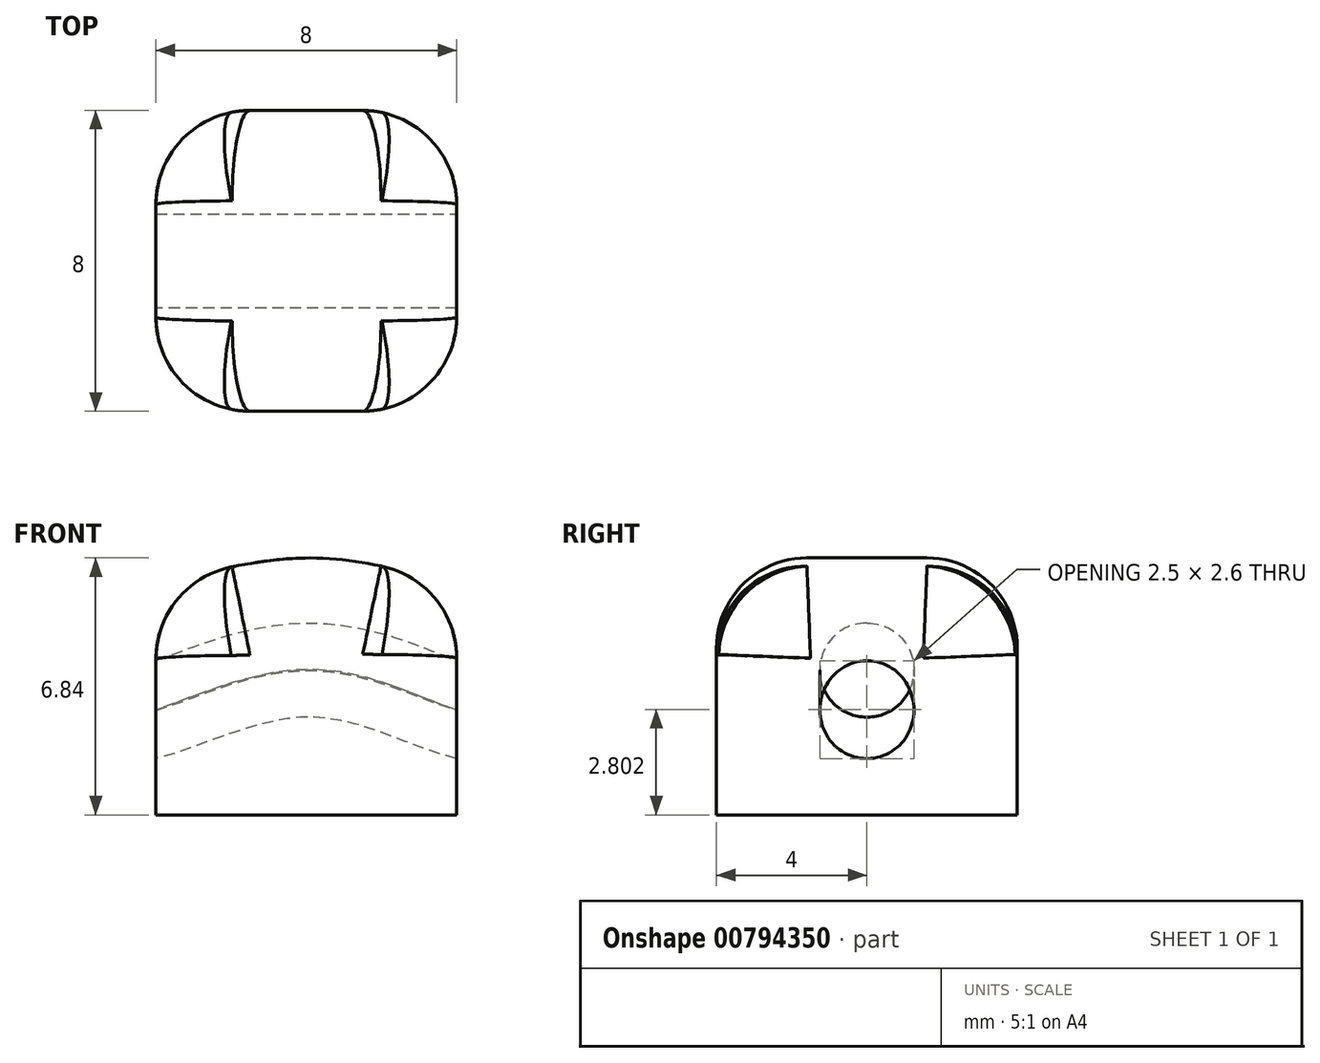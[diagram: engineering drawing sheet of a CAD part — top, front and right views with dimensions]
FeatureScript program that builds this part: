
annotation { "Feature Type Name" : "Feature", "Feature Type Description" : "" }
export const myFeature = defineFeature(function(context is Context, id is Id, definition is map)
    precondition{}
    {
        {
            var Q0;
            Q0=qCreatedBy(makeId("Front.planeOp"),FACE);
            var sketch = newSketch(context, id + "F0", { "sketchPlane" : qUnion([Q0])});
            skLineSegment(sketch, "E0.bottom", {"start": v(4, 10) * mm, "end": v(-4, 10) * mm, "construction": true});
            skLineSegment(sketch, "E0.top", {"start": v(4, -10) * mm, "end": v(-4, -10) * mm});
            skLineSegment(sketch, "E0.left", {"start": v(4, 10) * mm, "end": v(4, -10) * mm});
            skLineSegment(sketch, "E0.right", {"start": v(-4, 10) * mm, "end": v(-4, -10) * mm});
            skLineSegment(sketch, "E1", {"start": v(0, 10) * mm, "end": v(0, -10) * mm, "construction": true});
            skPoint(sketch, "E2", {"position": v(0, 0) * mm});
            skFitSpline(sketch, "E3", {"points": [v(4, -8.5) * mm, v(0, -7.4) * mm, v(-4, -8.5) * mm], "startDerivative": vector(-8.01, 1.98) * mm, "endDerivative": vector(-6.11, -1.33) * mm});
            skFitSpline(sketch, "E4.0", {"points": [v(4.6, -6.07) * mm, v(4.4, -6.02) * mm, v(3.92, -5.87) * mm, v(3.1, -5.54) * mm, v(2.28, -5.26) * mm, v(1.6, -5.07) * mm, v(0.95, -4.95) * mm, v(0.4, -4.9) * mm, v(-0.05, -4.9) * mm, v(-0.49, -4.92) * mm, v(-0.9, -4.97) * mm, v(-1.3, -5.04) * mm, v(-1.8, -5.15) * mm, v(-2.37, -5.31) * mm, v(-2.99, -5.52) * mm, v(-3.53, -5.72) * mm, v(-4, -5.9) * mm, v(-4.36, -6.01) * mm, v(-4.5, -6.05) * mm, v(-4.53, -6.06) * mm]});
            skFitSpline(sketch, "E5", {"points": [v(-4, -3.89) * mm, v(0, -3.16) * mm, v(4, -3.89) * mm], "startDerivative": vector(5.39, 1.32) * mm, "endDerivative": vector(6.83, -1.78) * mm});
            skSolve(sketch);
        }
        {
            var Q0;
            {var subQ0=sQuery(id+"F0.wireOp",EDGE,"E0.top");Q0=makeQuery(id+"F0.imprint","IMPRINT",FACE,{"disambiguationData":[TD([[makeQuery(id+"F0.imprint","IMPRINT",EDGE,{"derivedFrom":subQ0}),-1.0]])]});}
            var Q1;
            {var subQ0=sQuery(id+"F0.wireOp",EDGE,"E4.0");Q1=makeQuery(id+"F0.imprint","IMPRINT",FACE,{"disambiguationData":[TD([[makeQuery(id+"F0.imprint","IMPRINT",EDGE,{"derivedFrom":subQ0}),-1.0]])]});}
            var Q2;
            {var subQ0=sQuery(id+"F0.wireOp",EDGE,"E3");Q2=makeQuery(id+"F0.imprint","IMPRINT",FACE,{"disambiguationData":[TD([[makeQuery(id+"F0.imprint","IMPRINT",EDGE,{"derivedFrom":subQ0}),-1.0]])]});}
            extrude(context, id + "F1", {"entities" : qUnion([Q0, Q1, Q2]), "endBound" : BoundingType.SYMMETRIC, "depth" : 8 * mm, "offsetDistance" : 25 * mm});
        }
        {
            var Q0;
            {var subQ0=sQuery(id+"F0.wireOp",EDGE,"E3");Q0=makeQuery(id+"F0.imprint","IMPRINT",FACE,{"disambiguationData":[TD([[makeQuery(id+"F0.imprint","IMPRINT",EDGE,{"derivedFrom":subQ0}),-1.0]])]});}
            extrude(context, id + "F2", {"entities" : qUnion([Q0]), "operationType" : NewBodyOperationType.REMOVE, "endBound" : BoundingType.SYMMETRIC, "oppositeDirection" : true, "depth" : 2.5 * mm, "offsetDistance" : 25 * mm});
        }
        {
            var Q0;
            Q0=makeQuery(id+"F2.boolean.opBoolean","COPY",EDGE,{"derivedFrom":makeQuery(id+"F2.opExtrude","CAP_EDGE",EDGE,{"disambiguationData":[OSD([sQuery(id+"F0.wireOp",EDGE,"E4.0")])],"isStart":false})});
            var Q1;
            Q1=makeQuery(id+"F2.boolean.opBoolean","COPY",EDGE,{"derivedFrom":makeQuery(id+"F2.opExtrude","CAP_EDGE",EDGE,{"disambiguationData":[OSD([sQuery(id+"F0.wireOp",EDGE,"E4.0")])],"isStart":true})});
            var Q2;
            Q2=makeQuery(id+"F2.boolean.opBoolean","COPY",EDGE,{"derivedFrom":makeQuery(id+"F2.opExtrude","CAP_EDGE",EDGE,{"disambiguationData":[OSD([sQuery(id+"F0.wireOp",EDGE,"E3")])],"isStart":true})});
            var Q3;
            Q3=makeQuery(id+"F2.boolean.opBoolean","COPY",EDGE,{"derivedFrom":makeQuery(id+"F2.opExtrude","CAP_EDGE",EDGE,{"disambiguationData":[OSD([sQuery(id+"F0.wireOp",EDGE,"E3")])],"isStart":false})});
            fillet(context, id + "F3", {"entities" : qUnion([Q0, Q1, Q2, Q3]), "radius" : 1.24 * mm, "tangentPropagation" : true, "allowEdgeOverflow" : false});
        }
        {
            var Q0;
            Q0=makeQuery(id+"F1.opExtrude","CAP_EDGE",EDGE,{"disambiguationData":[OSD([sQuery(id+"F0.wireOp",EDGE,"E5")])],"isStart":false});
            var Q1;
            Q1=makeQuery(id+"F1.opExtrude","CAP_EDGE",EDGE,{"disambiguationData":[OSD([sQuery(id+"F0.wireOp",EDGE,"E5")])],"isStart":true});
            fillet(context, id + "F4", {"entities" : qUnion([Q0, Q1]), "radius" : 2.4 * mm, "tangentPropagation" : true, "allowEdgeOverflow" : false});
        }
        {
            var Q0;
            Q0=makeQuery(id+"F1.opExtrude","CAP_EDGE",EDGE,{"disambiguationData":[OSD([sQuery(id+"F0.wireOp",EDGE,"E0.right")])],"isStart":false});
            var Q1;
            Q1=makeQuery(id+"F4.opFillet","BLEND_EDGE",EDGE,{"blendedFrom":[makeQuery(id+"F1.opExtrude","CAP_EDGE",EDGE,{"disambiguationData":[OSD([sQuery(id+"F0.wireOp",EDGE,"E5")])],"isStart":false}),makeQuery(id+"F1.opExtrude","SWEPT_FACE",FACE,{"disambiguationData":[OSD([sQuery(id+"F0.wireOp",EDGE,"E0.right")])]})],"blendedInto":[makeQuery(id+"F1.opExtrude","SWEPT_FACE",FACE,{"disambiguationData":[OSD([sQuery(id+"F0.wireOp",EDGE,"E0.right")])]})]});
            var Q2;
            Q2=makeQuery(id+"F1.opExtrude","CAP_EDGE",EDGE,{"disambiguationData":[OSD([sQuery(id+"F0.wireOp",EDGE,"E0.right")])],"isStart":true});
            var Q3;
            Q3=makeQuery(id+"F4.opFillet","BLEND_EDGE",EDGE,{"blendedFrom":[makeQuery(id+"F1.opExtrude","CAP_EDGE",EDGE,{"disambiguationData":[OSD([sQuery(id+"F0.wireOp",EDGE,"E5")])],"isStart":true}),makeQuery(id+"F1.opExtrude","SWEPT_FACE",FACE,{"disambiguationData":[OSD([sQuery(id+"F0.wireOp",EDGE,"E0.right")])]})],"blendedInto":[makeQuery(id+"F1.opExtrude","SWEPT_FACE",FACE,{"disambiguationData":[OSD([sQuery(id+"F0.wireOp",EDGE,"E0.right")])]})]});
            var Q4;
            Q4=makeQuery(id+"F4.opFillet","BLEND_EDGE",EDGE,{"blendedFrom":[makeQuery(id+"F1.opExtrude","CAP_EDGE",EDGE,{"disambiguationData":[OSD([sQuery(id+"F0.wireOp",EDGE,"E5")])],"isStart":false}),makeQuery(id+"F1.opExtrude","SWEPT_FACE",FACE,{"disambiguationData":[OSD([sQuery(id+"F0.wireOp",EDGE,"E0.left")])]})],"blendedInto":[makeQuery(id+"F1.opExtrude","SWEPT_FACE",FACE,{"disambiguationData":[OSD([sQuery(id+"F0.wireOp",EDGE,"E0.left")])]})]});
            var Q5;
            Q5=makeQuery(id+"F4.opFillet","BLEND_EDGE",EDGE,{"blendedFrom":[makeQuery(id+"F1.opExtrude","CAP_EDGE",EDGE,{"disambiguationData":[OSD([sQuery(id+"F0.wireOp",EDGE,"E5")])],"isStart":true}),makeQuery(id+"F1.opExtrude","SWEPT_FACE",FACE,{"disambiguationData":[OSD([sQuery(id+"F0.wireOp",EDGE,"E0.left")])]})],"blendedInto":[makeQuery(id+"F1.opExtrude","SWEPT_FACE",FACE,{"disambiguationData":[OSD([sQuery(id+"F0.wireOp",EDGE,"E0.left")])]})]});
            var Q6;
            {var subQ0=sQuery(id+"F0.wireOp",EDGE,"E5");Q6=makeQuery(id+"F4.opFillet","BLEND_EDGE",EDGE,{"blendedFrom":[makeQuery(id+"F1.opExtrude","CAP_EDGE",EDGE,{"disambiguationData":[OSD([subQ0])],"isStart":true}),makeQuery(id+"F1.opExtrude","CAP_FACE",FACE,{"disambiguationData":[OSD([sQuery(id+"F0.wireOp",EDGE,"E0.top"),sQuery(id+"F0.wireOp",EDGE,"E0.left"),sQuery(id+"F0.wireOp",EDGE,"E0.right"),subQ0])],"isStart":true})],"blendedInto":[makeQuery(id+"F1.opExtrude","CAP_FACE",FACE,{"disambiguationData":[OSD([sQuery(id+"F0.wireOp",EDGE,"E0.top"),sQuery(id+"F0.wireOp",EDGE,"E0.left"),sQuery(id+"F0.wireOp",EDGE,"E0.right"),subQ0])],"isStart":true})]});}
            var Q7;
            {var subQ0=sQuery(id+"F0.wireOp",EDGE,"E5");Q7=makeQuery(id+"F4.opFillet","BLEND_EDGE",EDGE,{"blendedFrom":[makeQuery(id+"F1.opExtrude","CAP_EDGE",EDGE,{"disambiguationData":[OSD([subQ0])],"isStart":true}),makeQuery(id+"F1.opExtrude","SWEPT_FACE",FACE,{"disambiguationData":[OSD([subQ0])]})],"blendedInto":[makeQuery(id+"F1.opExtrude","SWEPT_FACE",FACE,{"disambiguationData":[OSD([subQ0])]})]});}
            var Q8;
            {var subQ0=sQuery(id+"F0.wireOp",EDGE,"E5");Q8=makeQuery(id+"F4.opFillet","BLEND_EDGE",EDGE,{"blendedFrom":[makeQuery(id+"F1.opExtrude","CAP_EDGE",EDGE,{"disambiguationData":[OSD([subQ0])],"isStart":false}),makeQuery(id+"F1.opExtrude","SWEPT_FACE",FACE,{"disambiguationData":[OSD([subQ0])]})],"blendedInto":[makeQuery(id+"F1.opExtrude","SWEPT_FACE",FACE,{"disambiguationData":[OSD([subQ0])]})]});}
            var Q9;
            {var subQ0=sQuery(id+"F0.wireOp",EDGE,"E5");Q9=makeQuery(id+"F4.opFillet","BLEND_EDGE",EDGE,{"blendedFrom":[makeQuery(id+"F1.opExtrude","CAP_EDGE",EDGE,{"disambiguationData":[OSD([subQ0])],"isStart":false}),makeQuery(id+"F1.opExtrude","CAP_FACE",FACE,{"disambiguationData":[OSD([sQuery(id+"F0.wireOp",EDGE,"E0.top"),sQuery(id+"F0.wireOp",EDGE,"E0.left"),sQuery(id+"F0.wireOp",EDGE,"E0.right"),subQ0])],"isStart":false})],"blendedInto":[makeQuery(id+"F1.opExtrude","CAP_FACE",FACE,{"disambiguationData":[OSD([sQuery(id+"F0.wireOp",EDGE,"E0.top"),sQuery(id+"F0.wireOp",EDGE,"E0.left"),sQuery(id+"F0.wireOp",EDGE,"E0.right"),subQ0])],"isStart":false})]});}
            var Q10;
            Q10=makeQuery(id+"F1.opExtrude","CAP_EDGE",EDGE,{"disambiguationData":[OSD([sQuery(id+"F0.wireOp",EDGE,"E0.left")])],"isStart":false});
            var Q11;
            Q11=makeQuery(id+"F1.opExtrude","CAP_EDGE",EDGE,{"disambiguationData":[OSD([sQuery(id+"F0.wireOp",EDGE,"E0.left")])],"isStart":true});
            var Q12;
            Q12=makeQuery(id+"F1.opExtrude","SWEPT_EDGE",EDGE,{"disambiguationData":[OSD([sQuery(id+"F0.wireOp",EDGE,"E0.left"),sQuery(id+"F0.wireOp",EDGE,"E5")])]});
            var Q13;
            Q13=makeQuery(id+"F1.opExtrude","SWEPT_EDGE",EDGE,{"disambiguationData":[OSD([sQuery(id+"F0.wireOp",EDGE,"E0.right"),sQuery(id+"F0.wireOp",EDGE,"E5")])]});
            fillet(context, id + "F5", {"entities" : qUnion([Q0, Q1, Q2, Q3, Q4, Q5, Q6, Q7, Q8, Q9, Q10, Q11, Q12, Q13]), "radius" : 2.5 * mm, "tangentPropagation" : true, "allowEdgeOverflow" : false});
        }
    });
